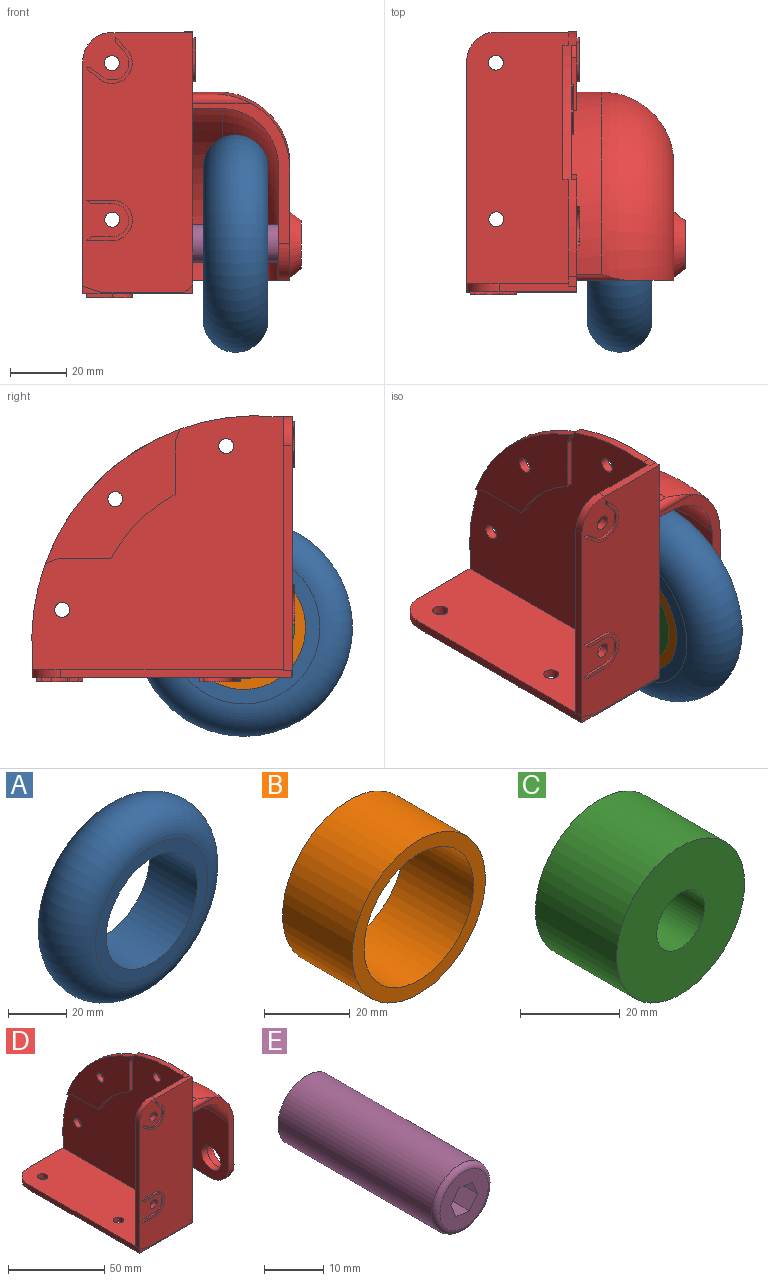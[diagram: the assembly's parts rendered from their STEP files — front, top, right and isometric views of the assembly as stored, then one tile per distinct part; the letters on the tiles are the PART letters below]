
ASSEMBLY  parts=5 mates=4
PART A: 4 faces, bbox 83.6x23x83.6 mm
  f0: cylinder r=22.01mm len=44.02mm, axis (0,1,0), area 3180.5mm2, adj f1,f2
  f1: plane 54.27x54.27mm, normal (0,-1,0), area 791.5mm2, adj f0,f3
  f2: plane 54.27x54.27mm, normal (0,1,0), area 791.5mm2, adj f0,f3
  f3: torus R=27.14mm, axis (0,-1,0), area 7821.6mm2, adj f1,f2
PART B: 4 faces, bbox 44x23x44 mm
  f0: cylinder r=22.01mm len=44.02mm, axis (0,1,0), area 3180.5mm2, adj f2,f3
  f1: cylinder r=18.11mm len=36.22mm, axis (0,1,0), area 2617.4mm2, adj f2,f3
  f2: plane 44.02x44.02mm, normal (0,-1,0), area 491.1mm2, adj f0,f1
  f3: plane 44.02x44.02mm, normal (0,1,0), area 491.1mm2, adj f0,f1
PART C: 4 faces, bbox 36.2x23x36.2 mm
  f0: cylinder r=18.11mm len=36.22mm, axis (0,1,0), area 2617.4mm2, adj f2,f3
  f1: cylinder r=6.76mm len=23mm, axis (0,1,0), area 976.8mm2, adj f2,f3
  f2: plane 36.22x36.22mm, normal (0,-1,0), area 887.1mm2, adj f0,f1
  f3: plane 36.22x36.22mm, normal (0,1,0), area 887.1mm2, adj f0,f1
PART D: 139 faces, bbox 82x131.6x130.1 mm
  f0: plane 92.35x39.07mm, normal (0,0,-1), area 3448.5mm2, adj f102,f103,f104,f105,f106,f109,f110,f111
  f1: plane 47.8x47.73mm, normal (1,0,0), area 816.8mm2, adj f10,f11,f12,f16,f17,f18,f69,f70
  f2: plane 39.55x29.57mm, normal (1,0,0), area 810.3mm2, adj f5,f7,f10,f15,f16,f17,f18,f39
  f3: plane 53.67x38.4mm, normal (0,-1,0), area 253.3mm2, adj f4,f8,f38,f40,f41,f43,f44,f45
  f4: cylinder r=13.15mm len=13.19mm, axis (-1,0,0), area 82.5mm2, adj f3,f5,f40,f44
  f5: plane 54.23x38.97mm, normal (0,0,-1), area 309.6mm2, adj f2,f4,f39,f40,f41,f43,f44,f45
  f6: cylinder r=7.01mm len=14.02mm, axis (-1,0,0), area 175.5mm2, adj f44,f48
  f7: plane 63.23x0.07mm, normal (0,0,-1), area 1.4mm2, adj f2,f15,f42,f45,f102,f103,f104,f106
  f8: plane 39.55x28mm, normal (1,0,0), area 806.8mm2, adj f3,f10,f11,f12,f13,f14,f16,f38
  f9: plane 90.07x89.45mm, normal (-1,0,0), area 5625mm2, adj f13,f15,f16,f19,f20,f21,f22,f23
  f10: cylinder r=55.81mm len=64.92mm, axis (-1,0,0), area 1009.1mm2, adj f1,f2,f8,f11,f18,f38,f39,f41
  f11: plane 18.71x2mm, normal (0,1,0), area 37.4mm2, adj f1,f8,f10,f12
  f12: plane 4.53x2mm, normal (0,0.94,0.35), area 9.7mm2, adj f1,f8,f11,f16
  f13: plane 3.29x3mm, normal (0,0,1), area 9.9mm2, adj f8,f9,f14,f16,f26
  f14: plane 68.75x0.08mm, normal (0,-1,0), area 1.7mm2, adj f8,f13,f29,f30,f35,f36,f42,f45
  f15: plane 3.3x3mm, normal (0,1,-0.03), area 9.1mm2, adj f2,f7,f9,f16,f104,f107
  f16: cylinder r=79.76mm len=87.16mm, axis (-1,0,0), area 422.6mm2, adj f1,f2,f8,f9,f12,f13,f15,f17
  f17: plane 4.53x2mm, normal (0,0.35,0.94), area 9.7mm2, adj f1,f2,f16,f18
  f18: plane 18.71x2mm, normal (0,0,1), area 37.4mm2, adj f1,f2,f10,f17
  f19: plane 4.53x2mm, normal (0,-0.94,-0.35), area 9.7mm2, adj f9,f16,f21,f24
  f20: plane 4.53x2mm, normal (0,-0.35,-0.94), area 9.7mm2, adj f9,f16,f23,f24
  f21: plane 18.71x2mm, normal (0,-1,0), area 37.4mm2, adj f9,f19,f22,f24
  f22: cylinder r=55.81mm len=22.86mm, axis (1,0,0), area 65.6mm2, adj f9,f21,f23,f24
  f23: plane 18.71x2mm, normal (0,0,-1), area 37.4mm2, adj f9,f20,f22,f24
  f24: plane 47.8x47.73mm, normal (-1,0,0), area 996.5mm2, adj f16,f19,f20,f21,f22,f23,f99
  f25: plane 16.11x15.88mm, normal (1,0,0), area 131.4mm2, adj f16,f68,f72,f73,f99
  f26: plane 27.55x3mm, normal (0,0,1), area 79.7mm2, adj f13,f28,f30,f31,f37
  f27: plane 2.98x2.24mm, normal (0.6,0,-0.8), area 0.1mm2, adj f34,f37,f42,f105
  f28: plane 89.81x36.06mm, normal (0,1,0), area 3169.7mm2, adj f9,f26,f31,f32,f97,f98,f107
  f29: plane 19.07x2mm, normal (1,0,0), area 38.1mm2, adj f14,f30,f36,f37
  f30: plane 6.51x2mm, normal (1,0,0), area 13mm2, adj f14,f26,f29,f37
  f31: cylinder r=10.17mm len=11.48mm, axis (0,-1,0), area 51.9mm2, adj f26,f28,f32,f37
  f32: plane 79.96x3.01mm, normal (-1,0,0), area 239.8mm2, adj f28,f31,f33,f37,f112
  f33: plane 6.79x2.23mm, normal (-0.31,0,-0.95), area 0.2mm2, adj f32,f34,f37,f105
  f34: plane 29.27x0.02mm, normal (0,0,-1), area 0.7mm2, adj f27,f33,f37,f105
  f35: plane 43.17x2.01mm, normal (1,0,0), area 85.5mm2, adj f14,f36,f37,f42
  f36: plane 2x0.06mm, normal (-0.02,0,-1), area 0.1mm2, adj f14,f29,f35,f37
  f37: plane 92.35x39.04mm, normal (0,-1,0), area 3437.1mm2, adj f26,f27,f29,f30,f31,f32,f33,f34
  f38: cylinder r=2.56mm len=20.71mm, axis (-1,0,0), area 64.6mm2, adj f3,f8,f10,f41
  f39: cylinder r=2.56mm len=20.71mm, axis (-1,0,0), area 64.6mm2, adj f2,f5,f10,f41
  f40: plane 41.41x41.4mm, normal (1,0,0), area 1033.8mm2, adj f3,f4,f5,f41,f47
  f41: torus R=30.22mm, axis (1,0,0), area 3880.7mm2, adj f3,f5,f10,f38,f39,f40
  f42: cone r=49.86mm half-angle=90deg, axis (-1,0,0), area 3546.1mm2, adj f7,f14,f27,f35,f37,f45,f105,f106
  f43: torus R=29.37mm, axis (1,0,0), area 2873.6mm2, adj f3,f5,f44,f45
  f44: plane 42.91x41.45mm, normal (-1,0,0), area 1369mm2, adj f3,f4,f5,f6,f43
  f45: cone r=49.69mm half-angle=0.9deg, axis (-1,0,0), area 1077.1mm2, adj f2,f3,f5,f7,f8,f14,f42,f43
  f46: plane 17.15x17.15mm, normal (1,0,0), area 77.4mm2, adj f47,f49
  f47: cone r=11.7mm half-angle=38deg, axis (-1,0,0), area 323.3mm2, adj f40,f46
  f48: plane 14.02x14.02mm, normal (-1,0,0), area 0.9mm2, adj f6,f49
  f49: cylinder r=6.99mm len=13.98mm, axis (-1,0,0), area 175.7mm2, adj f46,f48
  f50: plane 1.4x1.21mm, normal (0,0.76,0.65), area 1.9mm2, adj f8,f51,f57,f58
  f51: plane 9.8x1mm, normal (0,-1,0), area 9.8mm2, adj f8,f50,f52,f58
  f52: cylinder r=7mm len=13.8mm, axis (-1,0,0), area 19.6mm2, adj f8,f51,f53,f58
  f53: plane 8.26x1mm, normal (0,1,0), area 8.3mm2, adj f8,f52,f54,f58
  f54: plane 1.32x1mm, normal (0,-0.85,0.53), area 1.6mm2, adj f8,f53,f55,f58
  f55: plane 6.94x1mm, normal (0,-1,0), area 6.9mm2, adj f8,f54,f56,f58
  f56: cylinder r=5.99mm len=11.76mm, axis (-1,0,0), area 16.5mm2, adj f8,f55,f57,f58
  f57: plane 8.4x1mm, normal (0,1,0), area 8.4mm2, adj f8,f50,f56,f58
  f58: plane 15.64x13.8mm, normal (1,0,0), area 35.1mm2, adj f50,f51,f52,f53,f54,f55,f56,f57
  f59: plane 1.4x1.21mm, normal (0,0.65,0.76), area 1.9mm2, adj f2,f60,f66,f67
  f60: plane 8.4x1mm, normal (0,0,1), area 8.4mm2, adj f2,f59,f61,f67
  f61: cylinder r=5.99mm len=11.76mm, axis (-1,0,0), area 16.5mm2, adj f2,f60,f62,f67
  f62: plane 6.94x1mm, normal (0,0,-1), area 6.9mm2, adj f2,f61,f63,f67
  f63: plane 1.32x1mm, normal (0,0.53,-0.85), area 1.6mm2, adj f2,f62,f64,f67
  f64: plane 8.26x1mm, normal (0,0,1), area 8.3mm2, adj f2,f63,f65,f67
  f65: cylinder r=7mm len=13.8mm, axis (-1,0,0), area 19.6mm2, adj f2,f64,f66,f67
  f66: plane 9.8x1mm, normal (0,0,-1), area 9.8mm2, adj f2,f59,f65,f67
  f67: plane 15.65x13.81mm, normal (1,0,0), area 35.1mm2, adj f59,f60,f61,f62,f63,f64,f65,f66
  f68: plane 6.51x6.02mm, normal (0,0.73,-0.68), area 8.9mm2, adj f16,f25,f73,f74
  f69: plane 6.47x5.98mm, normal (0,-0.73,0.68), area 8.8mm2, adj f1,f16,f70,f74
  f70: cylinder r=7.02mm len=11.92mm, axis (-1,0,0), area 21.7mm2, adj f1,f69,f71,f74
  f71: plane 6.12x6.11mm, normal (0,0.71,-0.71), area 8.6mm2, adj f1,f16,f70,f74
  f72: plane 6.19x6.18mm, normal (0,-0.71,0.71), area 8.7mm2, adj f16,f25,f73,f74
  f73: cylinder r=5.72mm len=9.71mm, axis (-1,0,0), area 17.7mm2, adj f25,f68,f72,f74
  f74: plane 18.25x18.03mm, normal (1,0,0), area 48.4mm2, adj f16,f68,f69,f70,f71,f72,f73
  f75: plane 1x0.98mm, normal (0.74,0,0.67), area 1.3mm2, adj f37,f76,f84,f85
  f76: plane 1.8x1mm, normal (-1,0,0), area 1.8mm2, adj f37,f75,f77,f85
  f77: plane 3.33x3.09mm, normal (-0.73,0,-0.68), area 4.5mm2, adj f37,f76,f78,f85
  f78: cylinder r=5.99mm len=10.07mm, axis (0,1,0), area 17.9mm2, adj f37,f77,f79,f85
  f79: plane 3.87x3.07mm, normal (0.62,0,0.78), area 4.9mm2, adj f37,f78,f80,f85
  f80: plane 1.61x1mm, normal (0,0,1), area 1.6mm2, adj f37,f79,f81,f85
  f81: plane 1x0.94mm, normal (-0.73,0,-0.68), area 1.3mm2, adj f37,f80,f82,f85
  f82: plane 3.87x3.07mm, normal (-0.62,0,-0.78), area 4.9mm2, adj f37,f81,f83,f85
  f83: cylinder r=7.19mm len=12.08mm, axis (0,1,0), area 21.5mm2, adj f37,f82,f84,f85
  f84: plane 3.33x3.09mm, normal (0.73,0,0.68), area 4.5mm2, adj f37,f75,f83,f85
  f85: plane 16.4x16.39mm, normal (0,-1,0), area 36.6mm2, adj f75,f76,f77,f78,f79,f80,f81,f82
  f86: plane 9.25x1mm, normal (0,0,1), area 9.2mm2, adj f37,f87,f95,f96
  f87: plane 1x0.05mm, normal (-0.77,0,-0.64), area 0.1mm2, adj f37,f86,f88,f96
  f88: plane 1.79x1.3mm, normal (-0.59,0,-0.81), area 2.2mm2, adj f37,f87,f89,f96
  f89: plane 7.41x1mm, normal (0,0,-1), area 7.4mm2, adj f37,f88,f90,f96
  f90: cylinder r=5.86mm len=11.72mm, axis (0,1,0), area 18.4mm2, adj f37,f89,f91,f96
  f91: plane 7.41x1mm, normal (0,0,1), area 7.4mm2, adj f37,f90,f92,f96
  f92: plane 1.63x1.22mm, normal (-0.6,0,0.8), area 2mm2, adj f37,f91,f93,f96
  f93: plane 1x0.16mm, normal (-0.62,0,0.78), area 0.2mm2, adj f37,f92,f94,f96
  f94: plane 9.2x1mm, normal (0,0,-1), area 9.2mm2, adj f37,f93,f95,f96
  f95: cylinder r=7.21mm len=14.42mm, axis (0,1,0), area 22.7mm2, adj f37,f86,f94,f96
  f96: plane 16.46x14.42mm, normal (0,-1,0), area 50.2mm2, adj f86,f87,f88,f89,f90,f91,f92,f93
  f97: cylinder r=2.65mm len=5.3mm, axis (0,-1,0), area 50mm2, adj f28,f37
  f98: cylinder r=2.65mm len=5.3mm, axis (0,-1,0), area 50mm2, adj f28,f37
  f99: cylinder r=2.65mm len=5.3mm, axis (-1,0,0), area 50mm2, adj f24,f25
  f100: cylinder r=2.65mm len=5.3mm, axis (-1,0,0), area 50mm2, adj f2,f9
  f101: cylinder r=2.65mm len=5.3mm, axis (-1,0,0), area 50mm2, adj f8,f9
  f102: plane 2.72x0.06mm, normal (-0.02,-1,0), area 0.2mm2, adj f0,f7,f103,f106
  f103: plane 19.07x2.72mm, normal (1,0,0), area 51.8mm2, adj f0,f7,f102,f104
  f104: plane 6.52x3mm, normal (1,0,0), area 17.8mm2, adj f0,f7,f15,f103,f107,f109
  f105: plane 39.07x3mm, normal (0,-1,0), area 29.1mm2, adj f0,f27,f33,f34,f42,f108,f112,f113
  f106: plane 62.82x3mm, normal (1,0,0), area 177.6mm2, adj f0,f7,f42,f102,f108,f114
  f107: plane 89.37x39.03mm, normal (0,0,1), area 3154.2mm2, adj f9,f15,f28,f104,f109,f110,f111,f112
  f108: plane 28.65x0.04mm, normal (0,0,1), area 0.5mm2, adj f42,f105,f106,f113,f114
  f109: plane 3x2.97mm, normal (0,1,0), area 8.9mm2, adj f0,f104,f107,f110
  f110: plane 24.58x3mm, normal (0,1,0), area 73.7mm2, adj f0,f107,f109,f111
  f111: cylinder r=10.17mm len=11.48mm, axis (0,0,-1), area 51.9mm2, adj f0,f107,f110,f112
  f112: plane 82.18x3.01mm, normal (-1,0,0), area 245.6mm2, adj f0,f32,f105,f107,f111
  f113: plane 3x2.27mm, normal (1,0,0), area 6.8mm2, adj f0,f105,f108,f114
  f114: plane 3x1.59mm, normal (1,0,0), area 4.8mm2, adj f0,f106,f108,f113
  f115: plane 1.5x0.98mm, normal (0.74,0.67,0), area 2mm2, adj f0,f116,f124,f125
  f116: plane 1.8x1.5mm, normal (-1,0,0), area 2.7mm2, adj f0,f115,f117,f125
  f117: plane 3.33x3.09mm, normal (-0.73,-0.68,0), area 6.8mm2, adj f0,f116,f118,f125
  f118: cylinder r=5.99mm len=10.07mm, axis (0,0,1), area 26.9mm2, adj f0,f117,f119,f125
  f119: plane 3.87x3.07mm, normal (0.62,0.78,0), area 7.4mm2, adj f0,f118,f120,f125
  f120: plane 1.61x1.5mm, normal (0,1,0), area 2.4mm2, adj f0,f119,f121,f125
  f121: plane 1.5x0.94mm, normal (-0.73,-0.68,0), area 1.9mm2, adj f0,f120,f122,f125
  f122: plane 3.87x3.07mm, normal (-0.62,-0.78,0), area 7.4mm2, adj f0,f121,f123,f125
  f123: cylinder r=7.19mm len=12.08mm, axis (0,0,1), area 32.2mm2, adj f0,f122,f124,f125
  f124: plane 3.33x3.09mm, normal (0.73,0.68,0), area 6.8mm2, adj f0,f115,f123,f125
  f125: plane 16.4x16.39mm, normal (0,0,-1), area 36.6mm2, adj f115,f116,f117,f118,f119,f120,f121,f122
  f126: plane 9.25x1.5mm, normal (0,1,0), area 13.9mm2, adj f0,f127,f135,f136
  f127: plane 1.5x0.05mm, normal (-0.77,-0.64,0), area 0.1mm2, adj f0,f126,f128,f136
  f128: plane 1.79x1.5mm, normal (-0.59,-0.81,0), area 3.3mm2, adj f0,f127,f129,f136
  f129: plane 7.41x1.5mm, normal (0,-1,0), area 11.1mm2, adj f0,f128,f130,f136
  f130: cylinder r=5.86mm len=11.72mm, axis (0,0,1), area 27.6mm2, adj f0,f129,f131,f136
  f131: plane 7.41x1.5mm, normal (0,1,0), area 11.1mm2, adj f0,f130,f132,f136
  f132: plane 1.63x1.5mm, normal (-0.6,0.8,0), area 3.1mm2, adj f0,f131,f133,f136
  f133: plane 1.5x0.16mm, normal (-0.62,0.78,0), area 0.3mm2, adj f0,f132,f134,f136
  f134: plane 9.2x1.5mm, normal (0,-1,0), area 13.8mm2, adj f0,f133,f135,f136
  f135: cylinder r=7.21mm len=14.42mm, axis (0,0,1), area 34mm2, adj f0,f126,f134,f136
  f136: plane 16.46x14.42mm, normal (0,0,-1), area 50.2mm2, adj f126,f127,f128,f129,f130,f131,f132,f133
  f137: cylinder r=2.65mm len=5.3mm, axis (0,0,-1), area 50mm2, adj f0,f107
  f138: cylinder r=2.65mm len=5.3mm, axis (0,0,-1), area 50mm2, adj f0,f107
PART E: 10 faces, bbox 14.6x37.6x14.6 mm
  f0: plane 37.6x2.98mm, normal (0.92,0,0.38), area 121.5mm2, adj f1,f6,f7,f8
  f1: plane 37.6x2.57mm, normal (0.79,0,-0.61), area 121.5mm2, adj f0,f2,f7,f8
  f2: plane 37.6x3.21mm, normal (-0.13,0,-0.99), area 121.5mm2, adj f1,f3,f7,f8
  f3: plane 37.6x2.98mm, normal (-0.92,0,-0.38), area 121.5mm2, adj f2,f4,f7,f8
  f4: plane 37.6x2.57mm, normal (-0.79,0,0.61), area 121.5mm2, adj f3,f6,f7,f8
  f5: cylinder r=6.76mm len=36.6mm, axis (0,1,0), area 1554.4mm2, adj f8,f9
  f6: plane 37.6x3.21mm, normal (0.13,0,0.99), area 121.5mm2, adj f0,f4,f7,f8
  f7: plane 11.52x11.52mm, normal (0,-1,0), area 77.1mm2, adj f0,f1,f2,f3,f4,f6,f9
  f8: plane 13.52x13.52mm, normal (0,1,0), area 116.4mm2, adj f0,f1,f2,f3,f4,f5,f6
  f9: torus R=5.76mm, axis (0,-1,0), area 63.1mm2, adj f5,f7
PLACE A rot(axis=(0.58,-0.58,0.58),120deg) t=(88,-67.26,-59.35)mm
PLACE B rot(axis=(0.58,-0.58,0.58),120deg) t=(88,-67.26,-59.35)mm
PLACE C rot(axis=(0.58,-0.58,0.58),120deg) t=(88,-67.26,-59.35)mm
PLACE D t=(69.79,-36.25,-51.7)mm
PLACE E rot(axis=(0.58,-0.58,0.58),120deg) t=(91.5,-67.26,-59.35)mm
MATE revolute C.f0 <-> E.f5  axis (-1,0,0) through (88,-55.29,-73.89)mm
MATE fastened D.f4 <-> E.f5  axis (-1,0,0) through (103.3,-55.29,-73.89)mm
MATE fastened C.f0 <-> B.f0  axis (1,0,0) through (99.5,-55.29,-73.89)mm
MATE fastened B.f0 <-> A.f0  axis (1,0,0) through (99.5,-55.29,-73.89)mm
